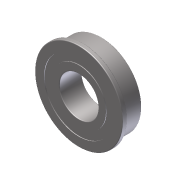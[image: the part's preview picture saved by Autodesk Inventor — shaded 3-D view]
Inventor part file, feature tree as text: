
AUTODESK INVENTOR PART (.ipt)
format: ipt  version: 2015 (Build 190159000, 159)  size: 197,120 bytes
history: native  units: in
note: dims shown in document units (in); Inventor stores cm internally (conversion verified against a paired STEP export)
features: fillet x1, other x1, imported_body x1
ambient origin geometry x8: Origin, YZ Plane, XZ Plane, XY Plane, X Axis, Y Axis, Z Axis, Center Point
bodies: Body1 (feature_tree)
feature tree (3):
  fillet  "Fillet1"  [1 undecoded]
  other  "217-4006-STEP-201408071"
  imported_body  "Base1"
note: 1 required parameter value undecoded (feature->parameter linkage not recoverable at this tier; creation-order binding heuristic only, values carry confidence <= 0.55)
